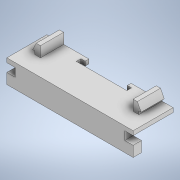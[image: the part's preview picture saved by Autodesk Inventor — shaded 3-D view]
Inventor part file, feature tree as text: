
AUTODESK INVENTOR PART (.ipt)
format: ipt  version: 2022.2 (Build 262287000, 287)  size: 201,216 bytes
history: native  units: mm
features: extrude x5, sketch x5
ambient origin geometry x8: Origin, YZ Plane, XZ Plane, XY Plane, X Axis, Y Axis, Z Axis, Center Point
bodies: Volumenkörper1 (feature_tree)
feature tree (10):
  extrude  "Extrusion1"  Depth=49.5mm
  extrude  "Extrusion2"  Depth=5.25mm
  extrude  "Extrusion3"  Depth=1.0mm
  extrude  "Extrusion4"  Depth=2.0mm
  extrude  "Extrusion5"  Depth=2.0mm
  sketch  "Skizze1"  dims[d0=49.5mm d1=24.75mm]
  sketch  "Skizze2"  dims[d2=5.25mm d3=5.25mm]
  sketch  "Skizze3"  dims[d4=1.0mm d5=1.0mm]
  sketch  "Skizze4"  dims[d6=44.0mm d7=2.0mm]
  sketch  "Skizze5"  dims[d8=22.0mm d9=2.0mm d10=5.0mm d11=2.0mm d12=2.0mm d13=1.5mm d14=11.0mm d15=0.0mm d16=9.0mm d17=4.0mm d18=2.0mm d19=2.0mm d20=2.0mm d21=11.0mm d22=0.0mm d23=4.0mm d24=2.0mm d25=57.0mm d26=28.5mm d27=10.0mm d28=0.0mm d29=20.0mm d30=2.0mm d31=2.0mm d32=2.2mm d33=1.8mm d34=10.0mm d35=10.0mm d36=0.0mm d37=4.0mm d38=4.0mm d39=4.0mm d40=10.0mm d41=0.0mm]
